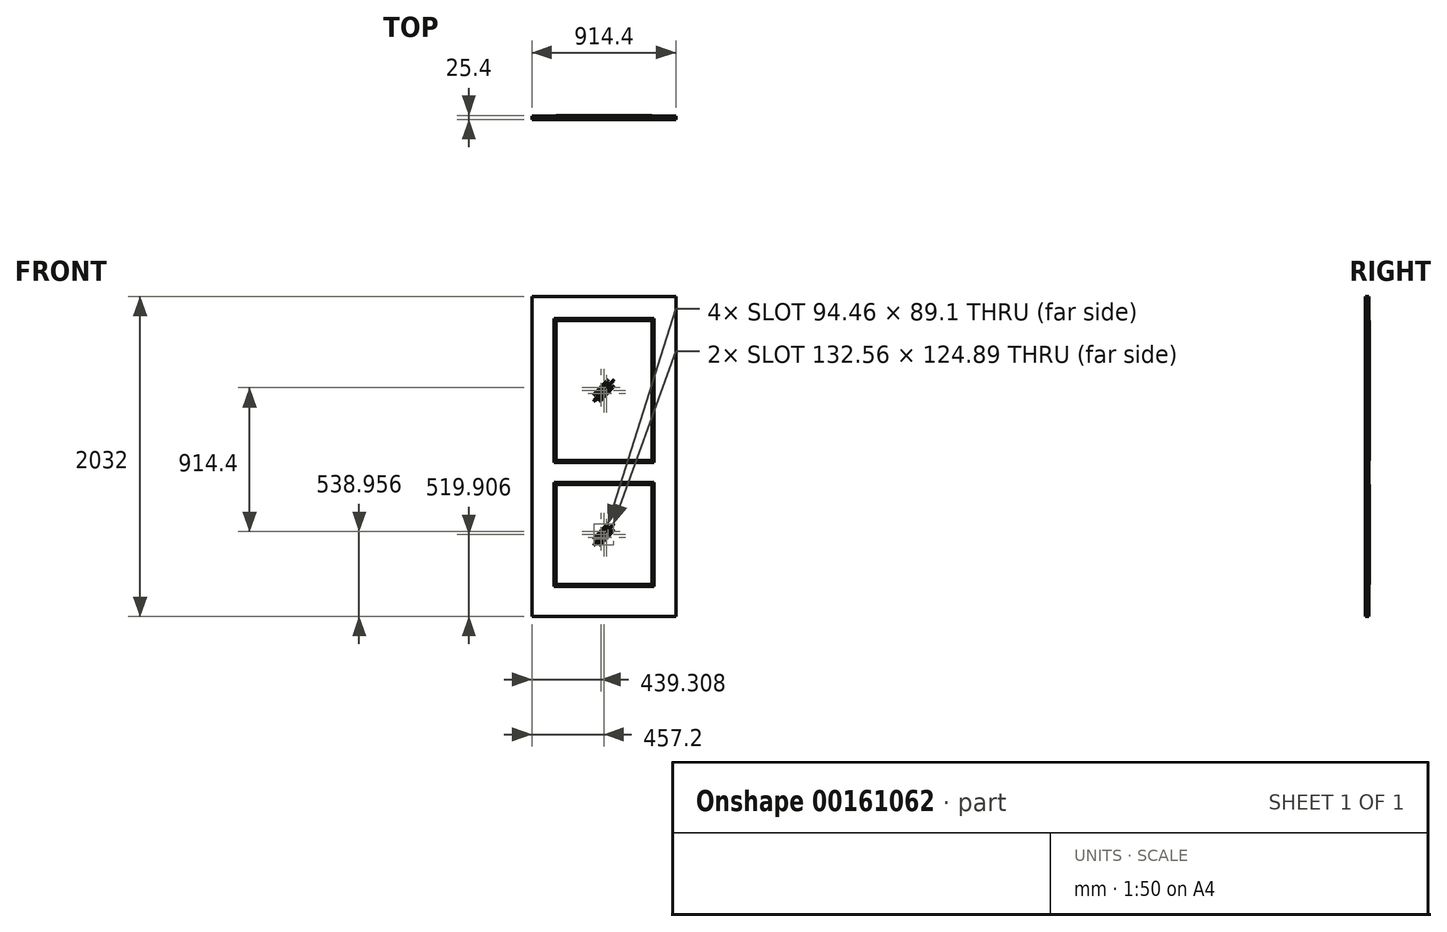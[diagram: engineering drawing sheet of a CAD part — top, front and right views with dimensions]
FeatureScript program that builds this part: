
annotation { "Feature Type Name" : "Feature", "Feature Type Description" : "" }
export const myFeature = defineFeature(function(context is Context, id is Id, definition is map)
    precondition{}
    {
        {
            var Q0;
            Q0=qCreatedBy(makeId("Front.planeOp"),FACE);
            var sketch = newSketch(context, id + "F0", { "sketchPlane" : qUnion([Q0])});
            skLineSegment(sketch, "E0.bottom", {"start": v(0, 0) * mm, "end": v(914.4, 0) * mm});
            skLineSegment(sketch, "E0.top", {"start": v(0, 2032) * mm, "end": v(914.4, 2032) * mm});
            skLineSegment(sketch, "E0.left", {"start": v(0, 0) * mm, "end": v(0, 2032) * mm});
            skLineSegment(sketch, "E0.right", {"start": v(914.4, 0) * mm, "end": v(914.4, 2032) * mm});
            skLineSegment(sketch, "E1.bottom", {"start": v(152.4, 203.2) * mm, "end": v(762, 203.2) * mm});
            skLineSegment(sketch, "E1.top", {"start": v(152.4, 836.61) * mm, "end": v(762, 836.61) * mm});
            skLineSegment(sketch, "E1.left", {"start": v(152.4, 203.2) * mm, "end": v(152.4, 836.61) * mm});
            skLineSegment(sketch, "E1.right", {"start": v(762, 203.2) * mm, "end": v(762, 836.61) * mm});
            skLineSegment(sketch, "E2.bottom", {"start": v(152.4, 989.01) * mm, "end": v(762, 989.01) * mm});
            skLineSegment(sketch, "E2.top", {"start": v(152.4, 1879.6) * mm, "end": v(762, 1879.6) * mm});
            skLineSegment(sketch, "E2.left", {"start": v(152.4, 989.01) * mm, "end": v(152.4, 1879.6) * mm});
            skLineSegment(sketch, "E2.right", {"start": v(762, 989.01) * mm, "end": v(762, 1879.6) * mm});
            skSolve(sketch);
        }
        {
            var Q0;
            Q0 = qSketchRegion(id + "F0", true);
            extrude(context, id + "F1", {"entities" : qUnion([Q0]), "depth" : 22.22 * mm, "hasSecondDirection" : true, "secondDirectionOppositeDirection" : true, "secondDirectionDepth" : 1.75 / 50.8 * mm});
        }
        {
            var Q0;
            Q0=qCreatedBy(makeId("Front.planeOp"),FACE);
            var sketch = newSketch(context, id + "F2", { "sketchPlane" : qUnion([Q0])});
            skLineSegment(sketch, "E3.0", {"start": v(152.4, 1879.6) * mm, "end": v(762, 1879.6) * mm});
            skLineSegment(sketch, "E4.0", {"start": v(152.4, 989.01) * mm, "end": v(152.4, 1879.6) * mm});
            skLineSegment(sketch, "E5.0", {"start": v(152.4, 989.01) * mm, "end": v(762, 989.01) * mm});
            skLineSegment(sketch, "E6.0", {"start": v(762, 989.01) * mm, "end": v(762, 1879.6) * mm});
            skLineSegment(sketch, "E7.0", {"start": v(762, 203.2) * mm, "end": v(762, 836.61) * mm});
            skLineSegment(sketch, "E8.0", {"start": v(152.4, 203.2) * mm, "end": v(762, 203.2) * mm});
            skLineSegment(sketch, "E9.0", {"start": v(152.4, 203.2) * mm, "end": v(152.4, 836.61) * mm});
            skLineSegment(sketch, "E10.0", {"start": v(152.4, 836.61) * mm, "end": v(762, 836.61) * mm});
            skLineSegment(sketch, "E11", {"start": v(516.47, 1497.41) * mm, "end": v(397.93, 1371.2) * mm});
            skLineSegment(sketch, "E12", {"start": v(480.69, 1497.41) * mm, "end": v(397.93, 1409.3) * mm});
            skLineSegment(sketch, "E13", {"start": v(516.47, 1459.31) * mm, "end": v(433.71, 1371.2) * mm});
            skLineSegment(sketch, "E14", {"start": v(516.47, 583.01) * mm, "end": v(397.93, 456.8) * mm});
            skLineSegment(sketch, "E15", {"start": v(480.69, 583.01) * mm, "end": v(397.93, 494.9) * mm});
            skLineSegment(sketch, "E16", {"start": v(516.47, 544.91) * mm, "end": v(433.71, 456.8) * mm});
            skArc(sketch, "E17.0.startCap", {"start": v(478.37, 1499.59) * mm, "mid": v(482.86, 1499.73) * mm, "end": v(483, 1495.24) * mm});
            skArc(sketch, "E17.0.endCap", {"start": v(400.24, 1407.13) * mm, "mid": v(395.76, 1406.99) * mm, "end": v(395.61, 1411.47) * mm});
            skLineSegment(sketch, "E17.0.left", {"start": v(483, 1495.24) * mm, "end": v(400.24, 1407.13) * mm});
            skLineSegment(sketch, "E17.0.right", {"start": v(478.37, 1499.59) * mm, "end": v(395.61, 1411.47) * mm});
            skArc(sketch, "E17.1.startCap", {"start": v(514.16, 1499.59) * mm, "mid": v(518.64, 1499.73) * mm, "end": v(518.79, 1495.24) * mm});
            skArc(sketch, "E17.1.endCap", {"start": v(400.24, 1369.03) * mm, "mid": v(395.76, 1368.89) * mm, "end": v(395.61, 1373.37) * mm});
            skLineSegment(sketch, "E17.1.left", {"start": v(518.79, 1495.24) * mm, "end": v(400.24, 1369.03) * mm});
            skLineSegment(sketch, "E17.1.right", {"start": v(514.16, 1499.59) * mm, "end": v(395.61, 1373.37) * mm});
            skArc(sketch, "E17.2.startCap", {"start": v(514.16, 1461.49) * mm, "mid": v(518.64, 1461.63) * mm, "end": v(518.79, 1457.14) * mm});
            skArc(sketch, "E17.2.endCap", {"start": v(436.03, 1369.03) * mm, "mid": v(431.54, 1368.89) * mm, "end": v(431.4, 1373.37) * mm});
            skLineSegment(sketch, "E17.2.left", {"start": v(518.79, 1457.14) * mm, "end": v(436.03, 1369.03) * mm});
            skLineSegment(sketch, "E17.2.right", {"start": v(514.16, 1461.49) * mm, "end": v(431.4, 1373.37) * mm});
            skArc(sketch, "E17.3.startCap", {"start": v(478.37, 585.19) * mm, "mid": v(482.86, 585.33) * mm, "end": v(483, 580.84) * mm});
            skArc(sketch, "E17.3.endCap", {"start": v(400.24, 492.73) * mm, "mid": v(395.76, 492.59) * mm, "end": v(395.61, 497.07) * mm});
            skLineSegment(sketch, "E17.3.left", {"start": v(483, 580.84) * mm, "end": v(400.24, 492.73) * mm});
            skLineSegment(sketch, "E17.3.right", {"start": v(478.37, 585.19) * mm, "end": v(395.61, 497.07) * mm});
            skArc(sketch, "E17.4.startCap", {"start": v(514.16, 585.19) * mm, "mid": v(518.64, 585.33) * mm, "end": v(518.79, 580.84) * mm});
            skArc(sketch, "E17.4.endCap", {"start": v(400.24, 454.63) * mm, "mid": v(395.76, 454.49) * mm, "end": v(395.61, 458.97) * mm});
            skLineSegment(sketch, "E17.4.left", {"start": v(518.79, 580.84) * mm, "end": v(400.24, 454.63) * mm});
            skLineSegment(sketch, "E17.4.right", {"start": v(514.16, 585.19) * mm, "end": v(395.61, 458.97) * mm});
            skArc(sketch, "E17.5.startCap", {"start": v(514.16, 547.09) * mm, "mid": v(518.64, 547.23) * mm, "end": v(518.79, 542.74) * mm});
            skArc(sketch, "E17.5.endCap", {"start": v(436.03, 454.63) * mm, "mid": v(431.54, 454.49) * mm, "end": v(431.4, 458.97) * mm});
            skLineSegment(sketch, "E17.5.left", {"start": v(518.79, 542.74) * mm, "end": v(436.03, 454.63) * mm});
            skLineSegment(sketch, "E17.5.right", {"start": v(514.16, 547.09) * mm, "end": v(431.4, 458.97) * mm});
            skSolve(sketch);
        }
        {
            var Q0;
            Q0 = qSketchRegion(id + "F2", true);
            extrude(context, id + "F3", {"entities" : qUnion([Q0]), "operationType" : NewBodyOperationType.ADD, "depth" : 3.17 * mm, "hasSecondDirection" : true, "secondDirectionOppositeDirection" : true, "secondDirectionDepth" : 3.17 * mm});
        }
        {
            var Q0;
            Q0=makeQuery(id+"F1.opExtrude","CAP_EDGE",EDGE,{"disambiguationData":[OSD([sQuery(id+"F0.wireOp",EDGE,"E2.top")])],"isStart":false});
            var Q1;
            Q1=makeQuery(id+"F1.opExtrude","CAP_EDGE",EDGE,{"disambiguationData":[OSD([sQuery(id+"F0.wireOp",EDGE,"E2.right")])],"isStart":false});
            var Q2;
            Q2=makeQuery(id+"F1.opExtrude","CAP_EDGE",EDGE,{"disambiguationData":[OSD([sQuery(id+"F0.wireOp",EDGE,"E2.bottom")])],"isStart":false});
            var Q3;
            Q3=makeQuery(id+"F1.opExtrude","CAP_EDGE",EDGE,{"disambiguationData":[OSD([sQuery(id+"F0.wireOp",EDGE,"E2.left")])],"isStart":false});
            var Q4;
            Q4=makeQuery(id+"F1.opExtrude","CAP_EDGE",EDGE,{"disambiguationData":[OSD([sQuery(id+"F0.wireOp",EDGE,"E1.top")])],"isStart":false});
            var Q5;
            Q5=makeQuery(id+"F1.opExtrude","CAP_EDGE",EDGE,{"disambiguationData":[OSD([sQuery(id+"F0.wireOp",EDGE,"E1.left")])],"isStart":false});
            var Q6;
            Q6=makeQuery(id+"F1.opExtrude","CAP_EDGE",EDGE,{"disambiguationData":[OSD([sQuery(id+"F0.wireOp",EDGE,"E1.right")])],"isStart":false});
            var Q7;
            Q7=makeQuery(id+"F1.opExtrude","CAP_EDGE",EDGE,{"disambiguationData":[OSD([sQuery(id+"F0.wireOp",EDGE,"E1.bottom")])],"isStart":false});
            var Q8;
            Q8=makeQuery(id+"F1.opExtrude","CAP_EDGE",EDGE,{"disambiguationData":[OSD([sQuery(id+"F0.wireOp",EDGE,"E1.top")])],"isStart":true});
            var Q9;
            Q9=makeQuery(id+"F1.opExtrude","CAP_EDGE",EDGE,{"disambiguationData":[OSD([sQuery(id+"F0.wireOp",EDGE,"E1.right")])],"isStart":true});
            var Q10;
            Q10=makeQuery(id+"F1.opExtrude","CAP_EDGE",EDGE,{"disambiguationData":[OSD([sQuery(id+"F0.wireOp",EDGE,"E1.left")])],"isStart":true});
            var Q11;
            Q11=makeQuery(id+"F1.opExtrude","CAP_EDGE",EDGE,{"disambiguationData":[OSD([sQuery(id+"F0.wireOp",EDGE,"E1.bottom")])],"isStart":true});
            var Q12;
            Q12=makeQuery(id+"F1.opExtrude","CAP_EDGE",EDGE,{"disambiguationData":[OSD([sQuery(id+"F0.wireOp",EDGE,"E2.left")])],"isStart":true});
            var Q13;
            Q13=makeQuery(id+"F1.opExtrude","CAP_EDGE",EDGE,{"disambiguationData":[OSD([sQuery(id+"F0.wireOp",EDGE,"E2.bottom")])],"isStart":true});
            var Q14;
            Q14=makeQuery(id+"F1.opExtrude","CAP_EDGE",EDGE,{"disambiguationData":[OSD([sQuery(id+"F0.wireOp",EDGE,"E2.right")])],"isStart":true});
            var Q15;
            Q15=makeQuery(id+"F1.opExtrude","CAP_EDGE",EDGE,{"disambiguationData":[OSD([sQuery(id+"F0.wireOp",EDGE,"E2.top")])],"isStart":true});
            chamfer(context, id + "F4", {"entities" : qUnion([Q0, Q1, Q2, Q3, Q4, Q5, Q6, Q7, Q8, Q9, Q10, Q11, Q12, Q13, Q14, Q15]), "width" : 12.7 * mm, "tangentPropagation" : true});
        }
    });
